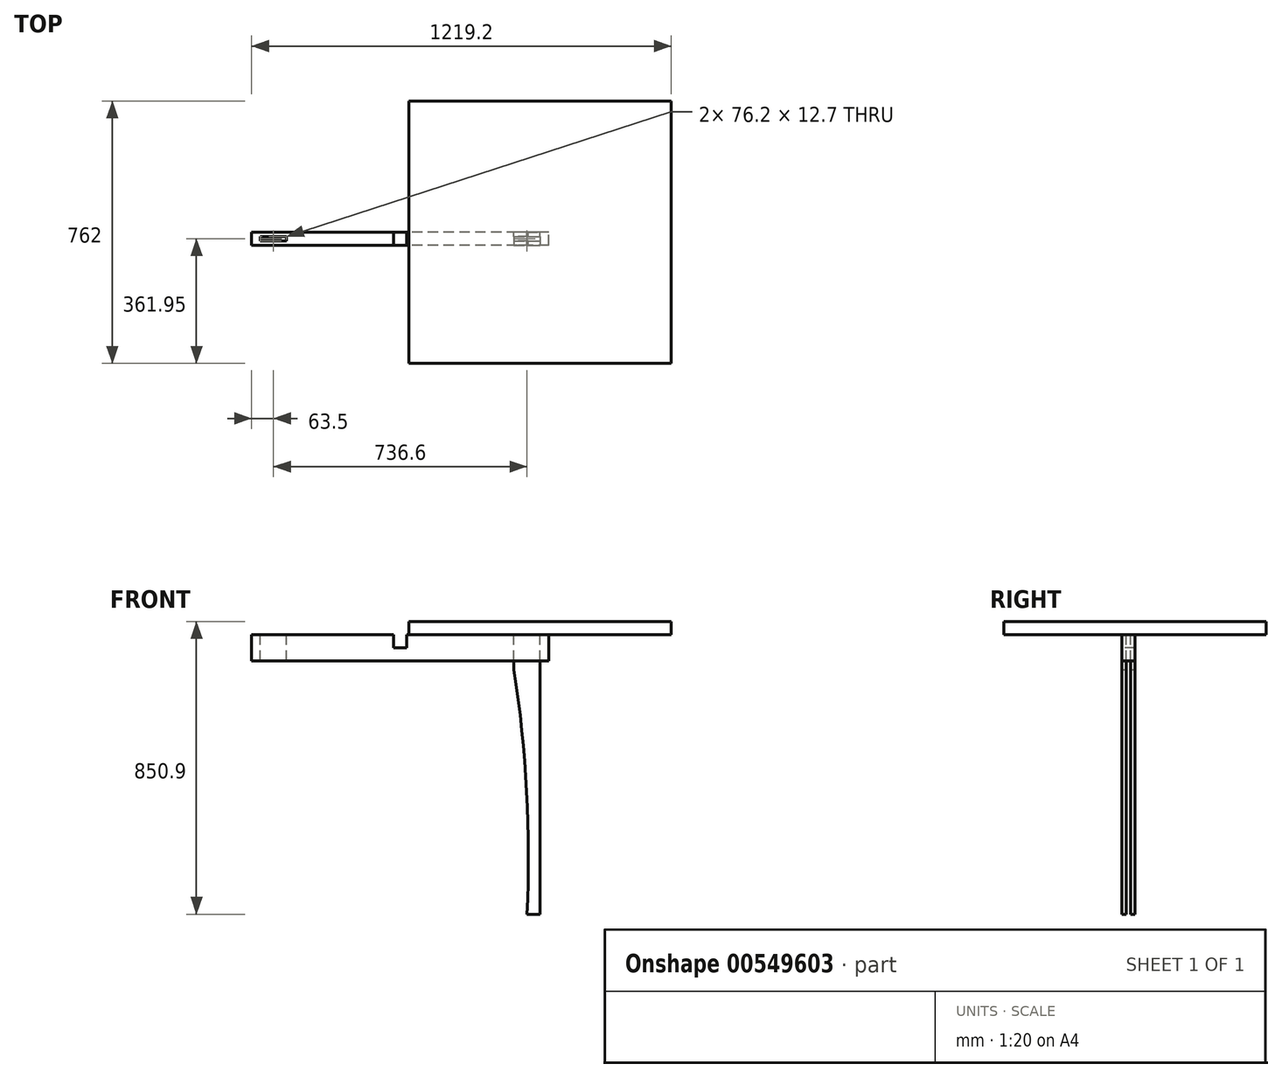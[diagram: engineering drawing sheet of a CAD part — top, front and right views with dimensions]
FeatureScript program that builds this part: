
annotation { "Feature Type Name" : "Feature", "Feature Type Description" : "" }
export const myFeature = defineFeature(function(context is Context, id is Id, definition is map)
    precondition{}
    {
        {
            var Q0;
            Q0=qCreatedBy(makeId("Front.planeOp"),FACE);
            var sketch = newSketch(context, id + "F0", { "sketchPlane" : qUnion([Q0])});
            skLineSegment(sketch, "E0.bottom", {"start": v(-76.2, 0) * mm, "end": v(0, 0) * mm});
            skLineSegment(sketch, "E0.top", {"start": v(-38.1, -812.8) * mm, "end": v(0, -812.8) * mm});
            skLineSegment(sketch, "E0.left", {"start": v(-76.2, 0) * mm, "end": v(-76.2, -101.6) * mm});
            skLineSegment(sketch, "E0.right", {"start": v(0, -101.6) * mm, "end": v(0, -812.8) * mm});
            skLineSegment(sketch, "E1", {"start": v(-76.2, -101.6) * mm, "end": v(0, -101.6) * mm});
            skArc(sketch, "E2", {"start": v(-38.1, -812.8) * mm, "mid": v(-39.3, -456.24) * mm, "end": v(-76.2, -101.6) * mm});
            skLineSegment(sketch, "E3", {"start": v(0, -101.6) * mm, "end": v(0, 0) * mm});
            skSolve(sketch);
        }
        {
            var Q0;
            Q0 = qSketchRegion(id + "F0", true);
            var Q1;
            Q1 = qConstructionFilter(qBodyType(qCreatedBy(id + "F0" ,EDGE), BodyType.WIRE), ConstructionObject.NO);
            extrude(context, id + "F1", {"entities" : qUnion([Q0]), "surfaceEntities" : qUnion([Q1]), "depth" : 38.1 * mm, "offsetDistance" : 25.4 * mm});
        }
        {
            var Q0;
            Q0=makeQuery(id+"F1.opExtrude","CAP_FACE",FACE,{"disambiguationData":[OSD([sQuery(id+"F0.wireOp",EDGE,"E0.bottom"),sQuery(id+"F0.wireOp",EDGE,"E0.top"),sQuery(id+"F0.wireOp",EDGE,"E0.left"),sQuery(id+"F0.wireOp",EDGE,"E0.right"),sQuery(id+"F0.wireOp",EDGE,"E2"),sQuery(id+"F0.wireOp",EDGE,"E3")])],"isStart":false});
            var sketch = newSketch(context, id + "F2", { "sketchPlane" : qUnion([Q0])});
            skLineSegment(sketch, "E4.bottom", {"start": v(-76.2, 0) * mm, "end": v(0, 0) * mm});
            skLineSegment(sketch, "E4.top", {"start": v(-76.2, -76.2) * mm, "end": v(0, -76.2) * mm});
            skLineSegment(sketch, "E4.left", {"start": v(-76.2, 0) * mm, "end": v(-76.2, -76.2) * mm});
            skLineSegment(sketch, "E4.right", {"start": v(0, 0) * mm, "end": v(0, -76.2) * mm});
            skSolve(sketch);
        }
        {
            var Q0;
            Q0 = qSketchRegion(id + "F2", true);
            extrude(context, id + "F3", {"entities" : qUnion([Q0]), "operationType" : NewBodyOperationType.REMOVE, "oppositeDirection" : true, "depth" : 12.7 * mm, "offsetDistance" : 25.4 * mm});
        }
        {
            var Q0;
            Q0=makeQuery(id+"F1.opExtrude","CAP_FACE",FACE,{"disambiguationData":[OSD([sQuery(id+"F0.wireOp",EDGE,"E0.bottom"),sQuery(id+"F0.wireOp",EDGE,"E0.top"),sQuery(id+"F0.wireOp",EDGE,"E0.left"),sQuery(id+"F0.wireOp",EDGE,"E0.right"),sQuery(id+"F0.wireOp",EDGE,"E2"),sQuery(id+"F0.wireOp",EDGE,"E3")])],"isStart":true});
            var sketch = newSketch(context, id + "F4", { "sketchPlane" : qUnion([Q0])});
            skLineSegment(sketch, "E5.bottom", {"start": v(0, 0) * mm, "end": v(76.2, 0) * mm});
            skLineSegment(sketch, "E5.top", {"start": v(0, -76.2) * mm, "end": v(76.2, -76.2) * mm});
            skLineSegment(sketch, "E5.left", {"start": v(0, 0) * mm, "end": v(0, -76.2) * mm});
            skLineSegment(sketch, "E5.right", {"start": v(76.2, 0) * mm, "end": v(76.2, -76.2) * mm});
            skSolve(sketch);
        }
        {
            var Q0;
            Q0 = qSketchRegion(id + "F4", true);
            extrude(context, id + "F5", {"entities" : qUnion([Q0]), "operationType" : NewBodyOperationType.REMOVE, "oppositeDirection" : true, "depth" : 12.7 * mm, "offsetDistance" : 25.4 * mm});
        }
        {
            var Q0;
            Q0=qCreatedBy(makeId("Front.planeOp"),FACE);
            var sketch = newSketch(context, id + "F6", { "sketchPlane" : qUnion([Q0])});
            skLineSegment(sketch, "E6.bottom", {"start": v(25.4, 0) * mm, "end": v(-838.2, 0) * mm});
            skLineSegment(sketch, "E6.top", {"start": v(25.4, -76.2) * mm, "end": v(-838.2, -76.2) * mm});
            skLineSegment(sketch, "E6.left", {"start": v(25.4, 0) * mm, "end": v(25.4, -76.2) * mm});
            skLineSegment(sketch, "E6.right", {"start": v(-838.2, 0) * mm, "end": v(-838.2, -76.2) * mm});
            skSolve(sketch);
        }
        {
            var Q0;
            Q0 = qSketchRegion(id + "F6", true);
            extrude(context, id + "F7", {"entities" : qUnion([Q0]), "depth" : 38.1 * mm, "offsetDistance" : 25.4 * mm});
        }
        {
            var Q0;
            Q0=makeQuery(id+"F7.opExtrude","SWEPT_FACE",FACE,{"disambiguationData":[OSD([sQuery(id+"F6.wireOp",EDGE,"E6.bottom")])]});
            var sketch = newSketch(context, id + "F8", { "sketchPlane" : qUnion([Q0])});
            skLineSegment(sketch, "E7.bottom", {"start": v(-76.2, -12.7) * mm, "end": v(0, -12.7) * mm});
            skLineSegment(sketch, "E7.top", {"start": v(-76.2, -25.4) * mm, "end": v(0, -25.4) * mm});
            skLineSegment(sketch, "E7.left", {"start": v(-76.2, -12.7) * mm, "end": v(-76.2, -25.4) * mm});
            skLineSegment(sketch, "E7.right", {"start": v(0, -12.7) * mm, "end": v(0, -25.4) * mm});
            skLineSegment(sketch, "E8", {"start": v(-38.1, -38.1) * mm, "end": v(-38.1, -25.4) * mm, "construction": true});
            skLineSegment(sketch, "E9", {"start": v(-38.1, -25.4) * mm, "end": v(-38.1, -12.7) * mm, "construction": true});
            skPoint(sketch, "E9.endSnap0", {"position": v(-38.1, -12.7) * mm});
            skLineSegment(sketch, "E10", {"start": v(-38.1, -12.7) * mm, "end": v(-38.1, 0) * mm, "construction": true});
            skLineSegment(sketch, "E11", {"start": v(-406.4, 0) * mm, "end": v(-406.4, -38.1) * mm, "construction": true});
            skLineSegment(sketch, "E12.MirrorCS", {"start": v(-736.6, -12.7) * mm, "end": v(-736.6, -25.4) * mm});
            skLineSegment(sketch, "E13.MirrorCS", {"start": v(-736.6, -25.4) * mm, "end": v(-812.8, -25.4) * mm});
            skLineSegment(sketch, "E14.MirrorCS", {"start": v(-812.8, -12.7) * mm, "end": v(-812.8, -25.4) * mm});
            skLineSegment(sketch, "E15.MirrorCS", {"start": v(-736.6, -12.7) * mm, "end": v(-812.8, -12.7) * mm});
            skSolve(sketch);
        }
        {
            var Q0;
            Q0 = qSketchRegion(id + "F8", true);
            extrude(context, id + "F9", {"entities" : qUnion([Q0]), "operationType" : NewBodyOperationType.REMOVE, "endBound" : BoundingType.THROUGH_ALL, "oppositeDirection" : true, "depth" : 25.4 * mm, "offsetDistance" : 25.4 * mm});
        }
        {
            var Q0;
            Q0=makeQuery(id+"F7.opExtrude","SWEPT_FACE",FACE,{"disambiguationData":[OSD([sQuery(id+"F6.wireOp",EDGE,"E6.bottom")])]});
            var sketch = newSketch(context, id + "F10", { "sketchPlane" : qUnion([Q0])});
            skLineSegment(sketch, "E16", {"start": v(-406.4, 0) * mm, "end": v(-406.4, -38.1) * mm, "construction": true});
            skLineSegment(sketch, "E17", {"start": v(-425.45, 0) * mm, "end": v(-425.45, -38.1) * mm});
            skLineSegment(sketch, "E18", {"start": v(-387.35, 0) * mm, "end": v(-387.35, -38.1) * mm});
            skLineSegment(sketch, "E19", {"start": v(-425.45, 0) * mm, "end": v(-406.4, 0) * mm});
            skLineSegment(sketch, "E20", {"start": v(-387.35, 0) * mm, "end": v(-406.4, 0) * mm});
            skLineSegment(sketch, "E21", {"start": v(-425.45, -38.1) * mm, "end": v(-406.4, -38.1) * mm});
            skLineSegment(sketch, "E22", {"start": v(-406.4, -38.1) * mm, "end": v(-387.35, -38.1) * mm});
            skSolve(sketch);
        }
        {
            var Q0;
            Q0 = qSketchRegion(id + "F10", true);
            extrude(context, id + "F11", {"entities" : qUnion([Q0]), "operationType" : NewBodyOperationType.REMOVE, "oppositeDirection" : true, "depth" : 38.1 * mm, "offsetDistance" : 25.4 * mm});
        }
        {
            var Q0;
            {var subQ0=sQuery(id+"F6.wireOp",EDGE,"E6.right");var subQ3=sQuery(id+"F6.wireOp",EDGE,"E6.bottom");Q0=makeQuery(id+"F11.boolean.opBoolean","SPLIT",FACE,{"disambiguationData":[TD([makeQuery(id+"F7.opExtrude","SWEPT_FACE",FACE,{"disambiguationData":[OSD([subQ0])]})])],"derivedFrom":makeQuery(id+"F7.opExtrude","SWEPT_FACE",FACE,{"disambiguationData":[OSD([subQ3])]})});}
            var sketch = newSketch(context, id + "F12", { "sketchPlane" : qUnion([Q0])});
            skLineSegment(sketch, "E23.bottom", {"start": v(-381, 381) * mm, "end": v(381, 381) * mm});
            skLineSegment(sketch, "E23.top", {"start": v(-381, -381) * mm, "end": v(381, -381) * mm});
            skLineSegment(sketch, "E23.left", {"start": v(-381, 381) * mm, "end": v(-381, -381) * mm});
            skLineSegment(sketch, "E23.right", {"start": v(381, 381) * mm, "end": v(381, -381) * mm});
            skLineSegment(sketch, "E24", {"start": v(0, 381) * mm, "end": v(0, 0) * mm, "construction": true});
            skLineSegment(sketch, "E25", {"start": v(-381, 0) * mm, "end": v(0, 0) * mm, "construction": true});
            skLineSegment(sketch, "E26", {"start": v(0, 0) * mm, "end": v(0, -381) * mm, "construction": true});
            skLineSegment(sketch, "E27", {"start": v(0, 0) * mm, "end": v(381, 0) * mm, "construction": true});
            skSolve(sketch);
        }
        {
            var Q0;
            Q0 = qSketchRegion(id + "F12", true);
            extrude(context, id + "F13", {"entities" : qUnion([Q0]), "depth" : 38.1 * mm, "offsetDistance" : 25.4 * mm});
        }
    });
